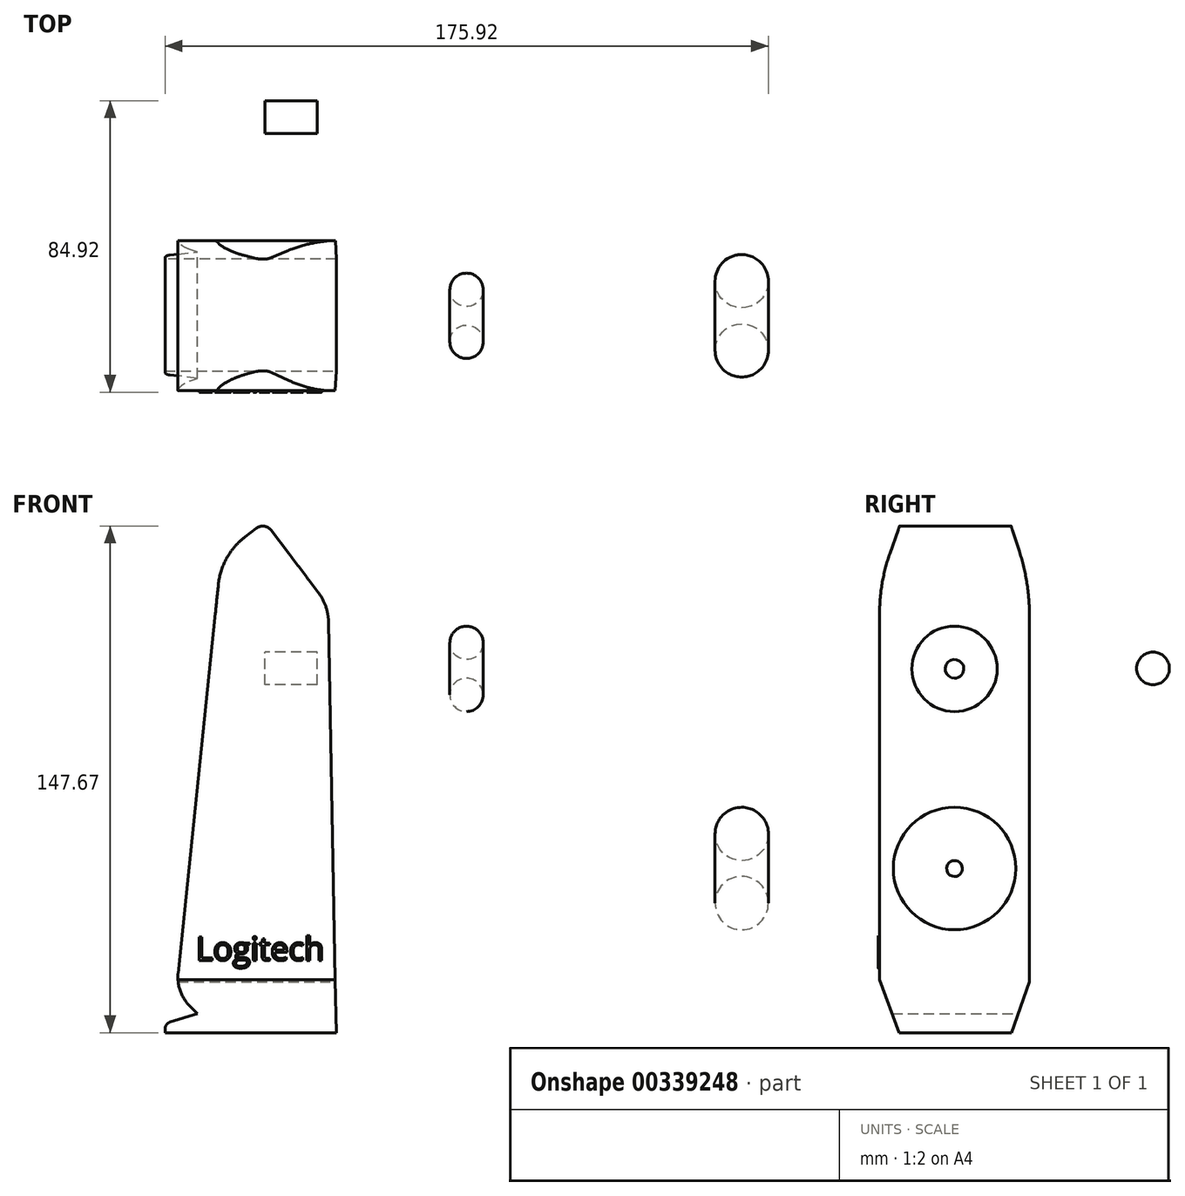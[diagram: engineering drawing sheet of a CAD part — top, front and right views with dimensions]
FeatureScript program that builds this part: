
annotation { "Feature Type Name" : "Feature", "Feature Type Description" : "" }
export const myFeature = defineFeature(function(context is Context, id is Id, definition is map)
    precondition{}
    {
        {
            var Q0;
            Q0=qCreatedBy(makeId("Front.planeOp"),FACE);
            var sketch = newSketch(context, id + "F0", { "sketchPlane" : qUnion([Q0])});
            skLineSegment(sketch, "E0", {"start": v(0, 72.98) * mm, "end": v(-12.63, 63.3) * mm});
            skLineSegment(sketch, "E1", {"start": v(-12.63, 63.3) * mm, "end": v(-25.85, -64.17) * mm});
            skLineSegment(sketch, "E2", {"start": v(-25.85, -64.17) * mm, "end": v(-19.68, -70.34) * mm});
            skLineSegment(sketch, "E3", {"start": v(-19.68, -70.34) * mm, "end": v(-29.08, -73.28) * mm});
            skLineSegment(sketch, "E4", {"start": v(-29.08, -73.28) * mm, "end": v(-29.08, -75.92) * mm});
            skLineSegment(sketch, "E5", {"start": v(-29.08, -75.92) * mm, "end": v(20.85, -75.92) * mm});
            skLineSegment(sketch, "E6", {"start": v(20.85, -75.92) * mm, "end": v(18.5, 48.6) * mm});
            skLineSegment(sketch, "E7", {"start": v(18.5, 48.6) * mm, "end": v(0, 72.98) * mm});
            skSolve(sketch);
        }
        {
            var Q0;
            Q0 = qSketchRegion(id + "F0", true);
            extrude(context, id + "F1", {"entities" : qUnion([Q0]), "endBound" : BoundingType.SYMMETRIC, "depth" : 43.69 * mm});
        }
        {
            var Q0;
            Q0=makeQuery(id+"F1.opExtrude","SWEPT_EDGE",EDGE,{"disambiguationData":[OSD([sQuery(id+"F0.wireOp",EDGE,"E6"),sQuery(id+"F0.wireOp",EDGE,"E7")])]});
            fillet(context, id + "F2", {"entities" : qUnion([Q0]), "radius" : 14.7 * mm, "tangentPropagation" : true, "allowEdgeOverflow" : false});
        }
        {
            var Q0;
            Q0=makeQuery(id+"F1.opExtrude","SWEPT_EDGE",EDGE,{"disambiguationData":[OSD([sQuery(id+"F0.wireOp",EDGE,"E0"),sQuery(id+"F0.wireOp",EDGE,"E7")])]});
            fillet(context, id + "F3", {"entities" : qUnion([Q0]), "radius" : 3.04 * mm, "tangentPropagation" : true, "allowEdgeOverflow" : false});
        }
        {
            var Q0;
            Q0=makeQuery(id+"F1.opExtrude","SWEPT_EDGE",EDGE,{"disambiguationData":[OSD([sQuery(id+"F0.wireOp",EDGE,"E0"),sQuery(id+"F0.wireOp",EDGE,"E1")])]});
            fillet(context, id + "F4", {"entities" : qUnion([Q0]), "radius" : 20.05 * mm, "tangentPropagation" : true, "allowEdgeOverflow" : false});
        }
        {
            var Q0;
            Q0=makeQuery(id+"F1.opExtrude","SWEPT_EDGE",EDGE,{"disambiguationData":[OSD([sQuery(id+"F0.wireOp",EDGE,"E1"),sQuery(id+"F0.wireOp",EDGE,"E2")])]});
            fillet(context, id + "F5", {"entities" : qUnion([Q0]), "radius" : 11.8 * mm, "tangentPropagation" : true, "allowEdgeOverflow" : false});
        }
        {
            var Q0;
            Q0=makeQuery(id+"F1.opExtrude","SWEPT_EDGE",EDGE,{"disambiguationData":[OSD([sQuery(id+"F0.wireOp",EDGE,"E3"),sQuery(id+"F0.wireOp",EDGE,"E4")])]});
            fillet(context, id + "F6", {"entities" : qUnion([Q0]), "radius" : 2.1 * mm, "tangentPropagation" : true, "allowEdgeOverflow" : false});
        }
        {
            var Q0;
            Q0=qCreatedBy(makeId("Right.planeOp"),FACE);
            var sketch = newSketch(context, id + "F7", { "sketchPlane" : qUnion([Q0])});
            skLineSegment(sketch, "E8", {"start": v(22.06, 54.6) * mm, "end": v(16.38, 72.14) * mm});
            skLineSegment(sketch, "E9", {"start": v(16.38, 72.14) * mm, "end": v(22.06, 72.14) * mm});
            skLineSegment(sketch, "E10", {"start": v(22.06, 72.14) * mm, "end": v(22.06, 54.6) * mm});
            skLineSegment(sketch, "E11", {"start": v(-22.09, 54.6) * mm, "end": v(-15.89, 72.14) * mm});
            skLineSegment(sketch, "E12", {"start": v(-15.89, 72.14) * mm, "end": v(-22.52, 72.14) * mm});
            skLineSegment(sketch, "E13", {"start": v(-22.52, 72.14) * mm, "end": v(-22.09, 54.6) * mm});
            skLineSegment(sketch, "E14", {"start": v(-22.52, -58.66) * mm, "end": v(-15.89, -76.56) * mm});
            skLineSegment(sketch, "E15", {"start": v(-15.89, -76.56) * mm, "end": v(-22.52, -76.56) * mm});
            skLineSegment(sketch, "E16", {"start": v(-22.52, -76.56) * mm, "end": v(-22.52, -58.66) * mm});
            skLineSegment(sketch, "E17", {"start": v(16.38, -76.56) * mm, "end": v(22.71, -58.66) * mm});
            skLineSegment(sketch, "E18", {"start": v(22.71, -58.66) * mm, "end": v(22.71, -76.56) * mm});
            skLineSegment(sketch, "E19", {"start": v(22.71, -76.56) * mm, "end": v(16.38, -76.56) * mm});
            skSolve(sketch);
        }
        {
            var Q0;
            Q0 = qSketchRegion(id + "F7", true);
            extrude(context, id + "F8", {"entities" : qUnion([Q0]), "operationType" : NewBodyOperationType.REMOVE, "endBound" : BoundingType.SYMMETRIC, "oppositeDirection" : true, "depth" : 91.95 * mm});
        }
        {
            var Q0;
            Q0=makeQuery(id+"F8.boolean.opBoolean","INTERSECT",EDGE,{"derivedFrom":[makeQuery(id+"F1.opExtrude","CAP_FACE",FACE,{"disambiguationData":[OSD([sQuery(id+"F0.wireOp",EDGE,"E0"),sQuery(id+"F0.wireOp",EDGE,"E1"),sQuery(id+"F0.wireOp",EDGE,"E2"),sQuery(id+"F0.wireOp",EDGE,"E3"),sQuery(id+"F0.wireOp",EDGE,"E4"),sQuery(id+"F0.wireOp",EDGE,"E5"),sQuery(id+"F0.wireOp",EDGE,"E6"),sQuery(id+"F0.wireOp",EDGE,"E7")])],"isStart":true}),makeQuery(id+"F8.opExtrude","SWEPT_FACE",FACE,{"disambiguationData":[OSD([sQuery(id+"F7.wireOp",EDGE,"E8")])]})]});
            fillet(context, id + "F9", {"entities" : qUnion([Q0]), "radius" : 61.48 * mm, "tangentPropagation" : true, "allowEdgeOverflow" : false});
        }
        {
            var Q0;
            Q0=makeQuery(id+"F8.boolean.opBoolean","INTERSECT",EDGE,{"derivedFrom":[makeQuery(id+"F1.opExtrude","CAP_FACE",FACE,{"disambiguationData":[OSD([sQuery(id+"F0.wireOp",EDGE,"E0"),sQuery(id+"F0.wireOp",EDGE,"E1"),sQuery(id+"F0.wireOp",EDGE,"E2"),sQuery(id+"F0.wireOp",EDGE,"E3"),sQuery(id+"F0.wireOp",EDGE,"E4"),sQuery(id+"F0.wireOp",EDGE,"E5"),sQuery(id+"F0.wireOp",EDGE,"E6"),sQuery(id+"F0.wireOp",EDGE,"E7")])],"isStart":false}),makeQuery(id+"F8.opExtrude","SWEPT_FACE",FACE,{"disambiguationData":[OSD([sQuery(id+"F7.wireOp",EDGE,"E11")])]})]});
            fillet(context, id + "F10", {"entities" : qUnion([Q0]), "radius" : 52.15 * mm, "tangentPropagation" : true, "allowEdgeOverflow" : false});
        }
        {
            var Q0;
            Q0=qCreatedBy(makeId("Front.planeOp"),FACE);
            var sketch = newSketch(context, id + "F11", { "sketchPlane" : qUnion([Q0])});
            skText(sketch, "E20", { "text": "Logitech", "fontName": "OpenSans-Regular.ttf"});
            const initialGuessF11  = {"E20": [-0.02003, -0.05485, 1, 0, 0.00685]};
            skSetInitialGuess(sketch, initialGuessF11);
            skSolve(sketch);
        }
        {
            var Q0;
            Q0 = qSketchRegion(id + "F11", true);
            extrude(context, id + "F12", {"entities" : qUnion([Q0]), "operationType" : NewBodyOperationType.ADD, "depth" : 22.28 * mm});
        }
        {
            var Q0;
            Q0=qCreatedBy(makeId("Front.planeOp"),FACE);
            var sketch = newSketch(context, id + "F13", { "sketchPlane" : qUnion([Q0])});
            skCircle(sketch, "E21", {"center": v(58.83, 37.7) * mm, "radius": 4.86 * mm});
            skCircle(sketch, "E22", {"center": v(139.07, -18) * mm, "radius": 7.77 * mm});
            skLineSegment(sketch, "E23", {"start": v(145.77, -28.07) * mm, "end": v(132.42, -28.07) * mm, "construction": true});
            skLineSegment(sketch, "E24", {"start": v(65.29, 30.12) * mm, "end": v(52.09, 30.12) * mm, "construction": true});
            skSolve(sketch);
        }
        {
            var Q0;
            Q0=makeQuery(id+"F13.imprint","IMPRINT",FACE,{"disambiguationData":[TD([[makeQuery(id+"F13.imprint","IMPRINT",EDGE,{"derivedFrom":sQuery(id+"F13.wireOp",EDGE,"E21")}),1.0]])]});
            var Q1;
            Q1=sQuery(id+"F13.wireOp",EDGE,"E24");
            revolve(context, id + "F14", {"entities" : qUnion([Q0]), "axis" : qUnion([Q1]), "revolveType" : RevolveType.FULL});
        }
        {
            var Q0;
            Q0=makeQuery(id+"F13.imprint","IMPRINT",FACE,{"disambiguationData":[TD([[makeQuery(id+"F13.imprint","IMPRINT",EDGE,{"derivedFrom":sQuery(id+"F13.wireOp",EDGE,"E22")}),1.0]])]});
            var Q1;
            Q1=sQuery(id+"F13.wireOp",EDGE,"E23");
            revolve(context, id + "F15", {"entities" : qUnion([Q0]), "axis" : qUnion([Q1]), "revolveType" : RevolveType.FULL});
        }
        {
            var Q0;
            Q0=qCreatedBy(makeId("Right.planeOp"),FACE);
            var sketch = newSketch(context, id + "F16", { "sketchPlane" : qUnion([Q0])});
            skCircle(sketch, "E25", {"center": v(57.87, 30.26) * mm, "radius": 4.77 * mm});
            skSolve(sketch);
        }
        {
            var Q0;
            Q0 = qSketchRegion(id + "F16", true);
            extrude(context, id + "F17", {"entities" : qUnion([Q0]), "depth" : 15.24 * mm});
        }
    });
